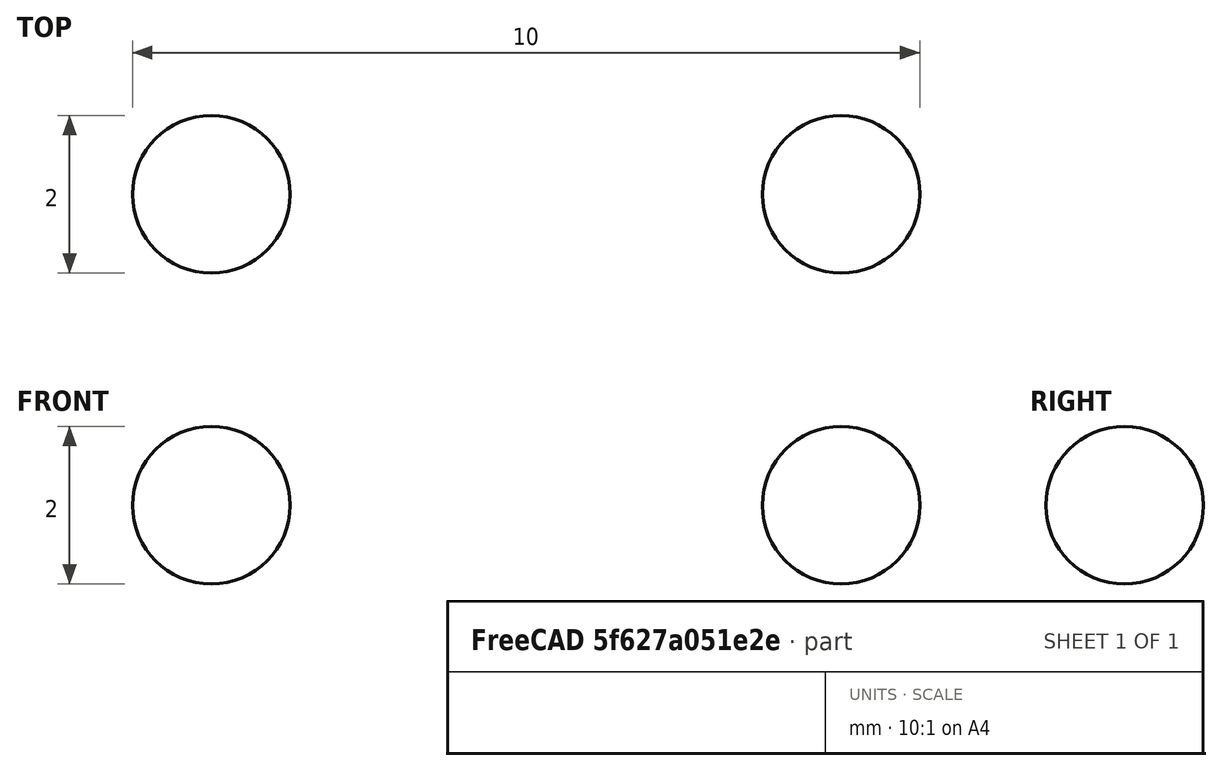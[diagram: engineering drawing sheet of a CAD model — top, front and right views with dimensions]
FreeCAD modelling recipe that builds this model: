
FCSTD DOCUMENT  (FreeCAD 0.22R37442 (Git))
Label: two-spheres
License: All rights reserved
LicenseURL: https://en.wikipedia.org/wiki/All_rights_reserved
objects: Part::Sphere×2, Part::FeaturePython×2
note: 4 computed .brp shape members not serialized (recipe doc carries the construction recipe); baked Part::Feature solids carry a one-line shape summary decoded from their .brp

FEATURE [Part::Sphere] Sphere
  Angle1 = -90
  Angle2 = 90
  Angle3 = 360
  AttacherType = Attacher::AttachEngine3D
  Placement = pos=(-4,0,0) rot=(0,0,1;0rad)
  Radius = 1
FEATURE [Part::Sphere] Sphere001
  Angle1 = -90
  Angle2 = 90
  Angle3 = 360
  AttacherType = Attacher::AttachEngine3D
  Placement = pos=(4,0,0) rot=(0,0,1;0rad)
  Radius = 1
FEATURE [Part::FeaturePython] BooleanFragments  # WARN: FeaturePython — macro-defined, semantics opaque (R4)
  Mode = 2
  Objects = -> [Sphere,Sphere001]
  Tolerance = 0
FEATURE [Part::FeaturePython] CompoundFilter  # WARN: FeaturePython — macro-defined, semantics opaque (R4)
  Base = -> BooleanFragments
  FilterType = 3
  Invert = false
  OverrideMaxVal = 0
  WindowFrom = 80
  WindowTo = 100
